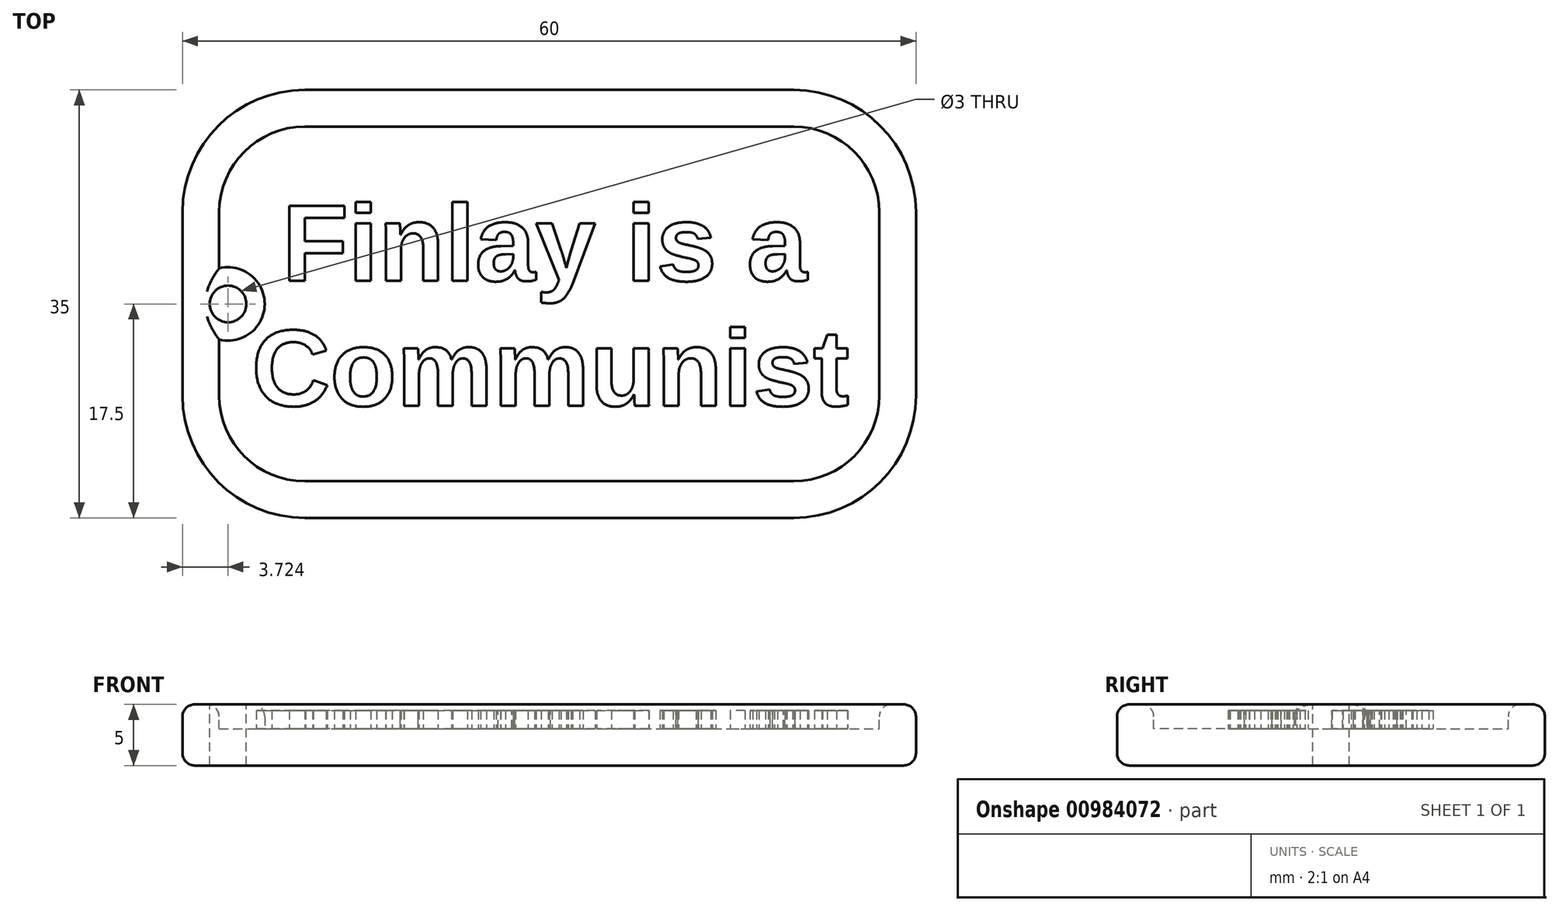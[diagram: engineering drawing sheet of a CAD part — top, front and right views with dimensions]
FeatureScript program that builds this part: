
annotation { "Feature Type Name" : "Feature", "Feature Type Description" : "" }
export const myFeature = defineFeature(function(context is Context, id is Id, definition is map)
    precondition{}
    {
        {
            var Q0;
            Q0=qCreatedBy(makeId("Top.planeOp"),FACE);
            var sketch = newSketch(context, id + "F0", { "sketchPlane" : qUnion([Q0])});
            skLineSegment(sketch, "E0.bottom", {"start": v(20, 17.5) * mm, "end": v(-20, 17.5) * mm});
            skLineSegment(sketch, "E0.top", {"start": v(20, -17.5) * mm, "end": v(-20, -17.5) * mm});
            skLineSegment(sketch, "E0.left", {"start": v(30, 7.5) * mm, "end": v(30, -7.5) * mm});
            skLineSegment(sketch, "E0.right", {"start": v(-30, 7.5) * mm, "end": v(-30, -7.5) * mm});
            skPoint(sketch, "E0.middle", {"position": v(0, 0) * mm});
            skPoint(sketch, "E1.visualSharp", {"position": v(30, 17.5) * mm});
            skArc(sketch, "E1.filletArc", {"start": v(30, 7.5) * mm, "mid": v(27.07, 14.57) * mm, "end": v(20, 17.5) * mm});
            skPoint(sketch, "E2.visualSharp", {"position": v(30, -17.5) * mm});
            skArc(sketch, "E2.filletArc", {"start": v(20, -17.5) * mm, "mid": v(27.07, -14.57) * mm, "end": v(30, -7.5) * mm});
            skPoint(sketch, "E3.visualSharp", {"position": v(-30, 17.5) * mm});
            skArc(sketch, "E3.filletArc", {"start": v(-20, 17.5) * mm, "mid": v(-27.07, 14.57) * mm, "end": v(-30, 7.5) * mm});
            skPoint(sketch, "E4.visualSharp", {"position": v(-30, -17.5) * mm});
            skArc(sketch, "E4.filletArc", {"start": v(-30, -7.5) * mm, "mid": v(-27.07, -14.57) * mm, "end": v(-20, -17.5) * mm});
            skSolve(sketch);
        }
        {
            var Q0;
            Q0=makeQuery(id+"F0.imprint","IMPRINT",FACE,{"disambiguationData":[TD([[makeQuery(id+"F0.imprint","IMPRINT",EDGE,{"derivedFrom":sQuery(id+"F0.wireOp",EDGE,"E0.bottom")}),1.0]])]});
            extrude(context, id + "F1", {"entities" : qUnion([Q0]), "depth" : 5 * mm, "offsetDistance" : 25 * mm});
        }
        {
            var Q0;
            Q0=makeQuery(id+"F1.opExtrude","CAP_FACE",FACE,{"disambiguationData":[OSD([sQuery(id+"F0.wireOp",EDGE,"E0.bottom"),sQuery(id+"F0.wireOp",EDGE,"E0.top"),sQuery(id+"F0.wireOp",EDGE,"E0.left"),sQuery(id+"F0.wireOp",EDGE,"E0.right"),sQuery(id+"F0.wireOp",EDGE,"E1.filletArc"),sQuery(id+"F0.wireOp",EDGE,"E2.filletArc"),sQuery(id+"F0.wireOp",EDGE,"E3.filletArc"),sQuery(id+"F0.wireOp",EDGE,"E4.filletArc")])],"isStart":false});
            var sketch = newSketch(context, id + "F2", { "sketchPlane" : qUnion([Q0])});
            skArc(sketch, "E5.0", {"start": v(20, -14.5) * mm, "mid": v(24.95, -12.45) * mm, "end": v(27, -7.5) * mm});
            skLineSegment(sketch, "E5.1", {"start": v(-20, -14.5) * mm, "end": v(20, -14.5) * mm});
            skLineSegment(sketch, "E5.2", {"start": v(27, -7.5) * mm, "end": v(27, 7.5) * mm});
            skArc(sketch, "E5.3", {"start": v(-27, -7.5) * mm, "mid": v(-24.95, -12.45) * mm, "end": v(-20, -14.5) * mm});
            skArc(sketch, "E5.4", {"start": v(27, 7.5) * mm, "mid": v(24.95, 12.45) * mm, "end": v(20, 14.5) * mm});
            skLineSegment(sketch, "E5.5", {"start": v(20, 14.5) * mm, "end": v(-20, 14.5) * mm});
            skArc(sketch, "E5.6", {"start": v(-20, 14.5) * mm, "mid": v(-24.95, 12.45) * mm, "end": v(-27, 7.5) * mm});
            skLineSegment(sketch, "E5.7", {"start": v(-27, 7.5) * mm, "end": v(-27, -7.5) * mm});
            skSolve(sketch);
        }
        {
            var Q0;
            Q0 = qSketchRegion(id + "F2", true);
            extrude(context, id + "F3", {"entities" : qUnion([Q0]), "operationType" : NewBodyOperationType.REMOVE, "oppositeDirection" : true, "depth" : 2 * mm, "offsetDistance" : 25 * mm});
        }
        {
            var Q0;
            Q0=makeQuery(id+"F3.boolean.opBoolean","COPY",FACE,{"derivedFrom":makeQuery(id+"F3.opExtrude","CAP_FACE",FACE,{"disambiguationData":[OSD([sQuery(id+"F2.wireOp",EDGE,"E5.0"),sQuery(id+"F2.wireOp",EDGE,"E5.1"),sQuery(id+"F2.wireOp",EDGE,"E5.2"),sQuery(id+"F2.wireOp",EDGE,"E5.3"),sQuery(id+"F2.wireOp",EDGE,"E5.4"),sQuery(id+"F2.wireOp",EDGE,"E5.5"),sQuery(id+"F2.wireOp",EDGE,"E5.6"),sQuery(id+"F2.wireOp",EDGE,"E5.7")])],"isStart":false})});
            var sketch = newSketch(context, id + "F4", { "sketchPlane" : qUnion([Q0])});
            skCircle(sketch, "E6", {"center": v(-26.28, 0) * mm, "radius": 3 * mm});
            skPoint(sketch, "E7", {"position": v(-27, 0) * mm});
            skSolve(sketch);
        }
        {
            var Q0;
            {var subQ0=sQuery(id+"F4.wireOp",EDGE,"E6");var subQ1=makeQuery(id+"F3.boolean.opBoolean","COPY",EDGE,{"derivedFrom":makeQuery(id+"F3.opExtrude","CAP_EDGE",EDGE,{"disambiguationData":[OSD([sQuery(id+"F2.wireOp",EDGE,"E5.7")])],"isStart":false})});var subQ2=makeQuery(id+"F4.imprint","INTERSECT",VERTEX,{"disambiguationData":[OD(0.0)],"derivedFrom":[subQ1,subQ0]});Q0=makeQuery(id+"F4.imprint","IMPRINT",FACE,{"disambiguationData":[TD([[makeQuery(id+"F4.imprint","IMPRINT",EDGE,{"disambiguationData":[TD([[subQ2,-1.0]])],"derivedFrom":subQ0}),1.0]])]});}
            extrude(context, id + "F5", {"entities" : qUnion([Q0]), "operationType" : NewBodyOperationType.ADD, "depth" : 2 * mm, "offsetDistance" : 25 * mm});
        }
        {
            var Q0;
            Q0=makeQuery(id+"F5.boolean.opBoolean","MERGE",FACE,{"derivedFrom":[makeQuery(id+"F1.opExtrude","CAP_FACE",FACE,{"disambiguationData":[OSD([sQuery(id+"F0.wireOp",EDGE,"E0.bottom"),sQuery(id+"F0.wireOp",EDGE,"E0.top"),sQuery(id+"F0.wireOp",EDGE,"E0.left"),sQuery(id+"F0.wireOp",EDGE,"E0.right"),sQuery(id+"F0.wireOp",EDGE,"E1.filletArc"),sQuery(id+"F0.wireOp",EDGE,"E2.filletArc"),sQuery(id+"F0.wireOp",EDGE,"E3.filletArc"),sQuery(id+"F0.wireOp",EDGE,"E4.filletArc")])],"isStart":false}),makeQuery(id+"F5.opExtrude","CAP_FACE",FACE,{"disambiguationData":[OSD([sQuery(id+"F2.wireOp",EDGE,"E5.7"),sQuery(id+"F4.wireOp",EDGE,"E6")])],"isStart":false})]});
            var Q1;
            Q1=makeQuery(id+"F1.opExtrude","CAP_FACE",FACE,{"disambiguationData":[OSD([sQuery(id+"F0.wireOp",EDGE,"E0.bottom"),sQuery(id+"F0.wireOp",EDGE,"E0.top"),sQuery(id+"F0.wireOp",EDGE,"E0.left"),sQuery(id+"F0.wireOp",EDGE,"E0.right"),sQuery(id+"F0.wireOp",EDGE,"E1.filletArc"),sQuery(id+"F0.wireOp",EDGE,"E2.filletArc"),sQuery(id+"F0.wireOp",EDGE,"E3.filletArc"),sQuery(id+"F0.wireOp",EDGE,"E4.filletArc")])],"isStart":true});
            fillet(context, id + "F6", {"entities" : qUnion([Q0, Q1]), "radius" : 1 * mm, "tangentPropagation" : true, "allowEdgeOverflow" : false});
        }
        {
            var Q0;
            Q0=makeQuery(id+"F3.boolean.opBoolean","COPY",FACE,{"derivedFrom":makeQuery(id+"F3.opExtrude","CAP_FACE",FACE,{"disambiguationData":[OSD([sQuery(id+"F2.wireOp",EDGE,"E5.0"),sQuery(id+"F2.wireOp",EDGE,"E5.1"),sQuery(id+"F2.wireOp",EDGE,"E5.2"),sQuery(id+"F2.wireOp",EDGE,"E5.3"),sQuery(id+"F2.wireOp",EDGE,"E5.4"),sQuery(id+"F2.wireOp",EDGE,"E5.5"),sQuery(id+"F2.wireOp",EDGE,"E5.6"),sQuery(id+"F2.wireOp",EDGE,"E5.7")])],"isStart":false})});
            var sketch = newSketch(context, id + "F7", { "sketchPlane" : qUnion([Q0])});
            skCircle(sketch, "E8", {"center": v(-26.28, 0) * mm, "radius": 1.5 * mm});
            skSolve(sketch);
        }
        {
            var Q0;
            Q0 = qSketchRegion(id + "F7", true);
            extrude(context, id + "F8", {"entities" : qUnion([Q0]), "operationType" : NewBodyOperationType.REMOVE, "endBound" : BoundingType.THROUGH_ALL, "oppositeDirection" : true, "depth" : 25 * mm, "offsetDistance" : 25 * mm, "hasSecondDirection" : true, "secondDirectionOppositeDirection" : false, "secondDirectionDepth" : 25 * mm});
        }
        {
            var Q0;
            Q0=makeQuery(id+"F3.boolean.opBoolean","COPY",FACE,{"derivedFrom":makeQuery(id+"F3.opExtrude","CAP_FACE",FACE,{"disambiguationData":[OSD([sQuery(id+"F2.wireOp",EDGE,"E5.0"),sQuery(id+"F2.wireOp",EDGE,"E5.1"),sQuery(id+"F2.wireOp",EDGE,"E5.2"),sQuery(id+"F2.wireOp",EDGE,"E5.3"),sQuery(id+"F2.wireOp",EDGE,"E5.4"),sQuery(id+"F2.wireOp",EDGE,"E5.5"),sQuery(id+"F2.wireOp",EDGE,"E5.6"),sQuery(id+"F2.wireOp",EDGE,"E5.7")])],"isStart":false})});
            var sketch = newSketch(context, id + "F9", { "sketchPlane" : qUnion([Q0])});
            skText(sketch, "E9", { "text": " Finlay is a\nCommunist", "fontName": "Arimo-Bold.ttf"});
            const initialGuessF9  = {"E9": [-0.02434, 0.0019, 1, 0, 0.0064]};
            skSetInitialGuess(sketch, initialGuessF9);
            skSolve(sketch);
        }
        {
            var Q0;
            Q0 = qSketchRegion(id + "F9", true);
            extrude(context, id + "F10", {"entities" : qUnion([Q0]), "operationType" : NewBodyOperationType.ADD, "depth" : 1.5 * mm, "offsetDistance" : 25 * mm});
        }
    });
